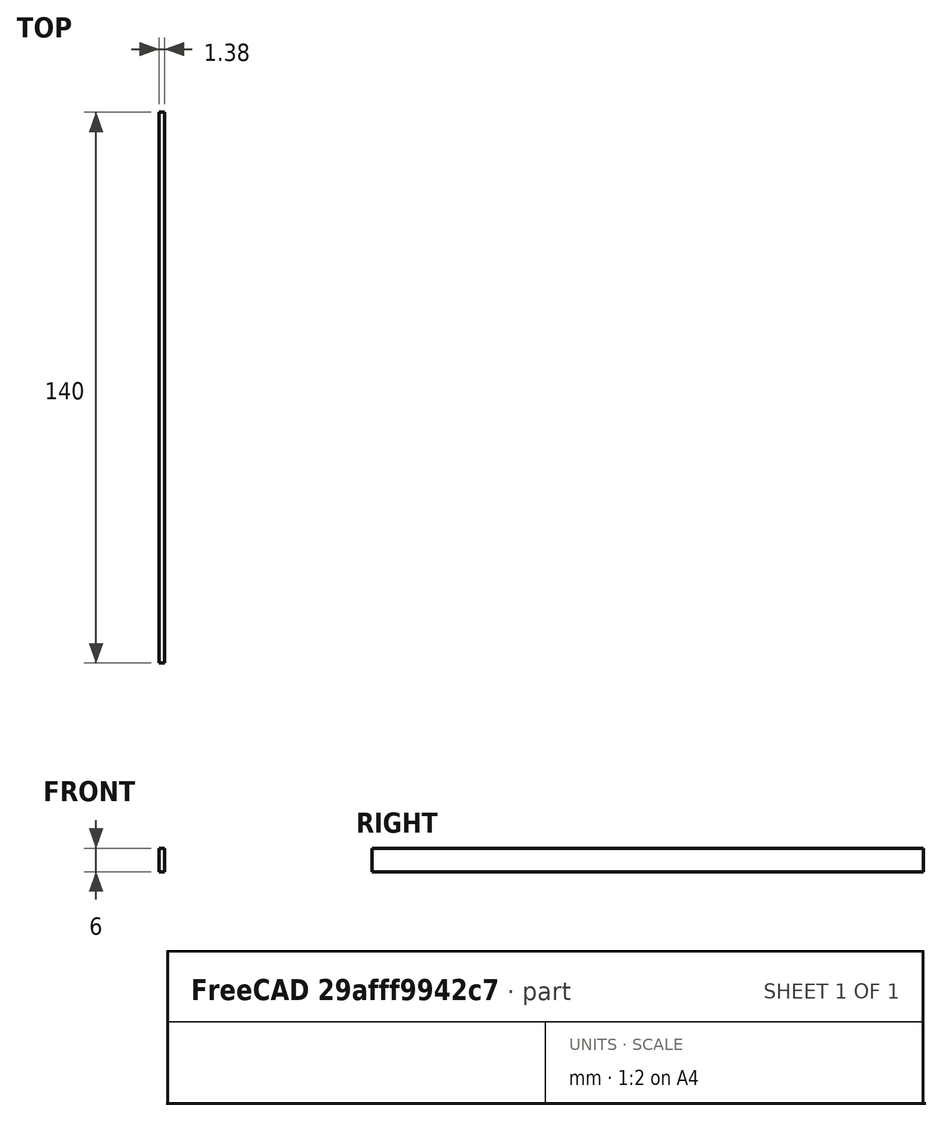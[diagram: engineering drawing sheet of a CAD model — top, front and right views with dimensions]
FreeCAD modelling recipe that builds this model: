
FCSTD DOCUMENT  (FreeCAD 0.20R27078 (Git))
Label: belt 140 mm
License: All rights reserved
LicenseURL: http://en.wikipedia.org/wiki/All_rights_reserved
objects: Sketcher::SketchObject×1, PartDesign::Pad×1, PartDesign::Body×1
note: 4 computed .brp shape members not serialized (recipe doc carries the construction recipe); baked Part::Feature solids carry a one-line shape summary decoded from their .brp

FEATURE [Sketcher::SketchObject] Sketch005
  FullyConstrained = true
  MapMode = 5
  Placement = pos=(0,0,0) rot=(1,0,0;1.5708rad)
  Support = -> [XZ_Plane003]
  sketch-geometry (4):
    g0: LineSegment StartX=0 StartY=6 StartZ=0 EndX=1.38 EndY=6 EndZ=0
    g1: LineSegment StartX=1.38 StartY=6 StartZ=0 EndX=1.38 EndY=0 EndZ=0
    g2: LineSegment StartX=1.38 StartY=0 StartZ=0 EndX=0 EndY=0 EndZ=0
    g3: LineSegment StartX=0 StartY=0 StartZ=0 EndX=0 EndY=6 EndZ=0
  constraints (12):
    c: Coincident(g0,g1)
    c: Coincident(g1,g2)
    c: Coincident(g2,g3)
    c: Coincident(g3,g0)
    c: Horizontal(g0)
    c: Horizontal(g2)
    c: Vertical(g1)
    c: Vertical(g3)
    c: PointOnObject(g0,g-2)
    c: PointOnObject(g1,g-1)
    c: DistanceY(g3,g3) = 6
    c: DistanceX(g0,g0) = 1.38
FEATURE [PartDesign::Pad] Pad001
  Direction = (0,-1,-2e-16)
  Length = 140
  Length2 = 100
  Placement = pos=(0,0,0) rot=(1,0,0;1.5708rad)
  Profile = -> Sketch005
  ReferenceAxis = -> Sketch005 [N_Axis]
  Type = 0
FEATURE [PartDesign::Body] Body003  label="belt 140 mm"
  Group = -> [Sketch005,Pad001]
  Origin = -> Origin003
  Tip = -> Pad001
